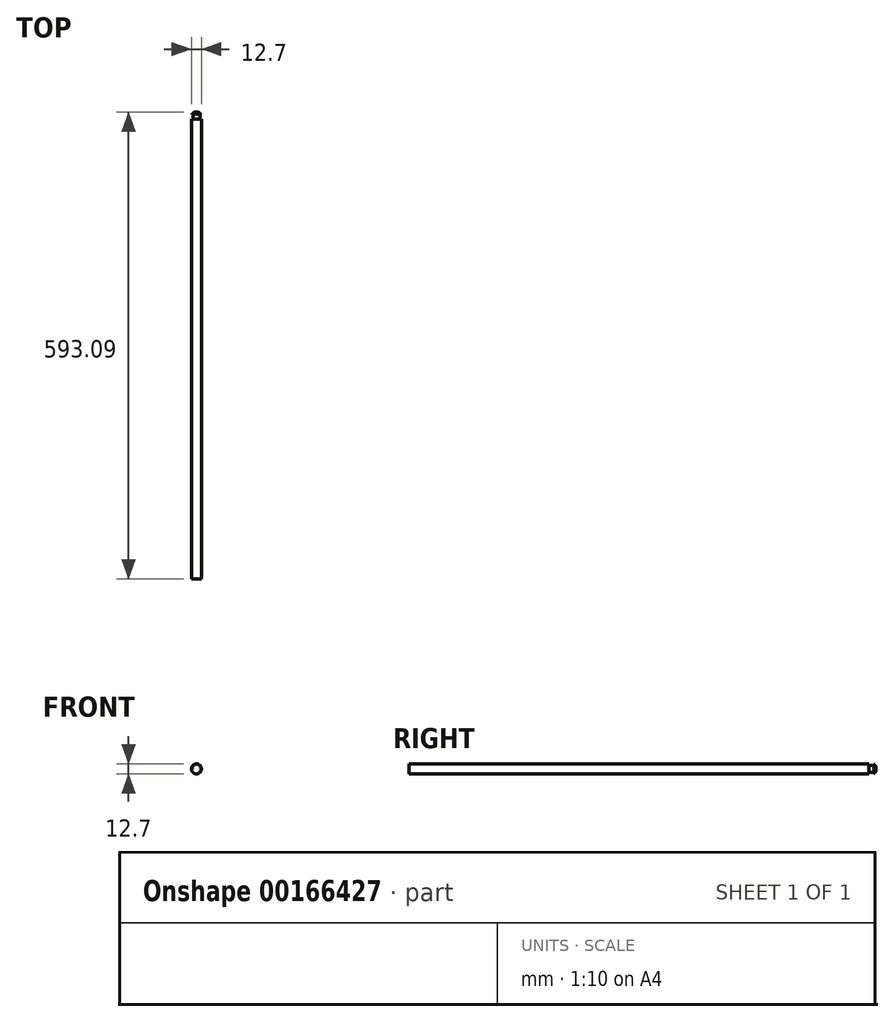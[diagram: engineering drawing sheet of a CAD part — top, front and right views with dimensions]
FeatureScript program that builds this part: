
annotation { "Feature Type Name" : "Feature", "Feature Type Description" : "" }
export const myFeature = defineFeature(function(context is Context, id is Id, definition is map)
    precondition{}
    {
        {
            var Q0;
            Q0=qCreatedBy(makeId("Front.planeOp"),FACE);
            var sketch = newSketch(context, id + "F0", { "sketchPlane" : qUnion([Q0])});
            skCircle(sketch, "E0", {"center": v(0, 0) * mm, "radius": 6.35 * mm});
            skSolve(sketch);
        }
        {
            var Q0;
            Q0 = qSketchRegion(id + "F0", true);
            extrude(context, id + "F1", {"entities" : qUnion([Q0]), "depth" : 584.2 * mm});
        }
        {
            var Q0;
            Q0=makeQuery(id+"F1.opExtrude","CAP_FACE",FACE,{"disambiguationData":[OSD([sQuery(id+"F0.wireOp",EDGE,"E0")])],"isStart":true});
            var sketch = newSketch(context, id + "F2", { "sketchPlane" : qUnion([Q0])});
            skCircle(sketch, "E1", {"center": v(0, 0) * mm, "radius": 4.62 * mm});
            skSolve(sketch);
        }
        {
            var Q0;
            Q0=makeQuery(id+"F2.imprint","IMPRINT",FACE,{"disambiguationData":[TD([[makeQuery(id+"F2.imprint","IMPRINT",EDGE,{"derivedFrom":sQuery(id+"F2.wireOp",EDGE,"E1")}),1.0]])]});
            var Q1;
            Q1=sQuery(id+"F2.wireOp",EDGE,"E1");
            extrude(context, id + "F3", {"entities" : qUnion([Q0]), "surfaceEntities" : qUnion([Q1]), "depth" : 6.35 * mm});
        }
        {
            var Q0;
            Q0=makeQuery(id+"F3.opExtrude","CAP_FACE",FACE,{"disambiguationData":[OSD([sQuery(id+"F2.wireOp",EDGE,"E1")])],"isStart":false});
            var sketch = newSketch(context, id + "F4", { "sketchPlane" : qUnion([Q0])});
            skCircle(sketch, "E2", {"center": v(0, 0) * mm, "radius": 5.53 * mm});
            skSolve(sketch);
        }
        {
            var Q0;
            Q0 = qSketchRegion(id + "F4", true);
            extrude(context, id + "F5", {"entities" : qUnion([Q0]), "operationType" : NewBodyOperationType.ADD, "depth" : 2.54 * mm});
        }
        {
            var Q0;
            Q0=makeQuery(id+"F5.opExtrude","CAP_EDGE",EDGE,{"disambiguationData":[OSD([sQuery(id+"F4.wireOp",EDGE,"E2")])],"isStart":false});
            fillet(context, id + "F6", {"entities" : qUnion([Q0]), "radius" : 5.08 * mm, "tangentPropagation" : true, "allowEdgeOverflow" : false});
        }
    });
